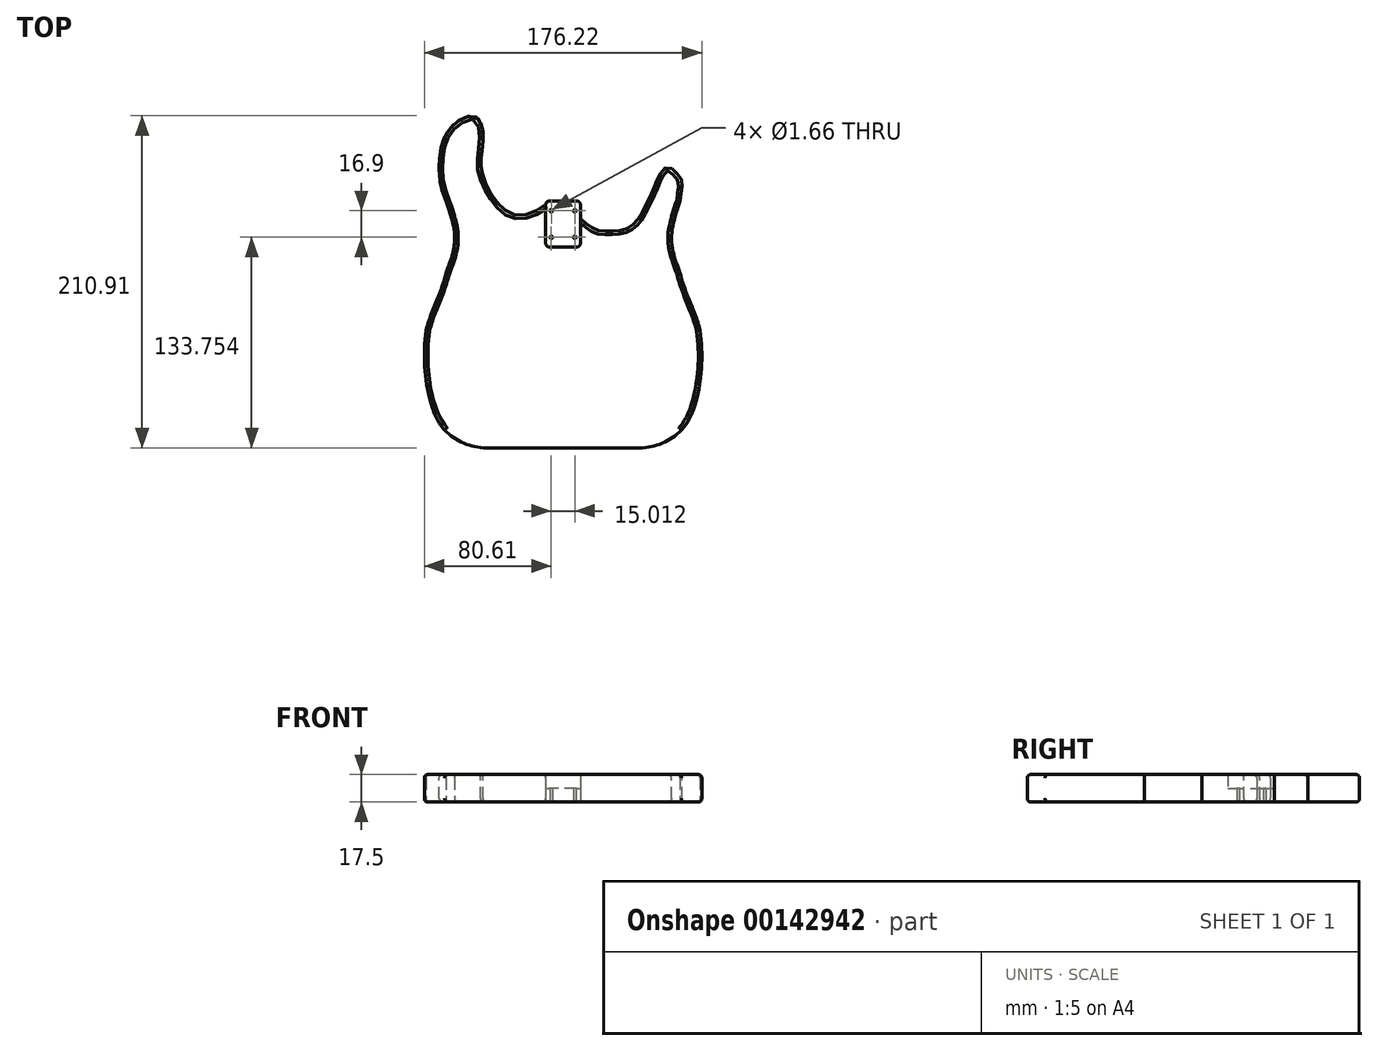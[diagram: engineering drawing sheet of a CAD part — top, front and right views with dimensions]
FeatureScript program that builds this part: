
annotation { "Feature Type Name" : "Feature", "Feature Type Description" : "" }
export const myFeature = defineFeature(function(context is Context, id is Id, definition is map)
    precondition{}
    {
        {
            var Q0;
            Q0=qCreatedBy(makeId("Top.planeOp"),FACE);
            var sketch = newSketch(context, id + "F0", { "sketchPlane" : qUnion([Q0])});
            skLineSegment(sketch, "E0", {"start": v(-48.7, -35.3) * mm, "end": v(0, -35.3) * mm});
            skArc(sketch, "E1", {"start": v(-75.2, -24.05) * mm, "mid": v(-63.1, -32.38) * mm, "end": v(-48.7, -35.3) * mm});
            skLineSegment(sketch, "E2.MirrorCS", {"start": v(48.7, -35.3) * mm, "end": v(0, -35.3) * mm});
            skArc(sketch, "E3.MirrorCS", {"start": v(75.2, -24.05) * mm, "mid": v(63.1, -32.38) * mm, "end": v(48.7, -35.3) * mm});
            skLineSegment(sketch, "E4", {"start": v(0, -35.3) * mm, "end": v(0, 202.55) * mm, "construction": true});
            skLineSegment(sketch, "E5.bottom", {"start": v(8.5, 92.2) * mm, "end": v(-8.5, 92.2) * mm});
            skLineSegment(sketch, "E5.top", {"start": v(8.5, 121.57) * mm, "end": v(-8.5, 121.57) * mm});
            skLineSegment(sketch, "E5.left", {"start": v(11, 94.7) * mm, "end": v(11, 119.07) * mm});
            skLineSegment(sketch, "E5.right", {"start": v(-11, 94.7) * mm, "end": v(-11, 119.07) * mm});
            skPoint(sketch, "E5.middle", {"position": v(0, 106.88) * mm});
            skPoint(sketch, "E6", {"position": v(11, 110.3) * mm});
            skCircle(sketch, "E7", {"center": v(-7.5, 98.44) * mm, "radius": 0.83 * mm});
            skLineSegment(sketch, "E8", {"start": v(-11, 106.9) * mm, "end": v(11, 106.88) * mm, "construction": true});
            skCircle(sketch, "E9.MirrorC", {"center": v(7.5, 98.44) * mm, "radius": 0.83 * mm});
            skLineSegment(sketch, "E10.MirrorCS", {"start": v(11, 106.9) * mm, "end": v(-11, 106.88) * mm, "construction": true});
            skCircle(sketch, "E11.MirrorC", {"center": v(-7.49, 115.34) * mm, "radius": 0.83 * mm});
            skCircle(sketch, "E12.MirrorC", {"center": v(7.51, 115.32) * mm, "radius": 0.83 * mm});
            skFitSpline(sketch, "E13", {"points": [v(-75.2, -24.05) * mm, v(-87, 7.11) * mm, v(-86.97, 39.1) * mm], "startDerivative": vector(-39.42, 41.67) * mm, "endDerivative": vector(8.43, 65.14) * mm});
            skFitSpline(sketch, "E14", {"points": [v(-86.97, 39.1) * mm, v(-74.37, 75.63) * mm], "startDerivative": vector(7.39, 34.16) * mm, "endDerivative": vector(7.39, 34.16) * mm});
            skFitSpline(sketch, "E15", {"points": [v(-74.37, 75.63) * mm, v(-68.78, 97.16) * mm, v(-74.37, 121.57) * mm], "startDerivative": vector(15.15, 40.9) * mm, "endDerivative": vector(-14.7, 44.2) * mm});
            skArc(sketch, "E16.filletArc", {"start": v(-8.5, 121.57) * mm, "mid": v(-10.27, 120.83) * mm, "end": v(-11, 119.07) * mm});
            skPoint(sketch, "E17.visualSharp", {"position": v(11, 121.57) * mm});
            skArc(sketch, "E17.filletArc", {"start": v(11, 119.07) * mm, "mid": v(10.27, 120.83) * mm, "end": v(8.5, 121.57) * mm});
            skPoint(sketch, "E18.visualSharp", {"position": v(11, 92.2) * mm});
            skArc(sketch, "E18.filletArc", {"start": v(8.5, 92.2) * mm, "mid": v(10.27, 92.93) * mm, "end": v(11, 94.7) * mm});
            skPoint(sketch, "E19.visualSharp", {"position": v(-11, 92.2) * mm});
            skArc(sketch, "E19.filletArc", {"start": v(-11, 94.7) * mm, "mid": v(-10.27, 92.93) * mm, "end": v(-8.5, 92.2) * mm});
            skFitSpline(sketch, "E20.MirrorCS", {"points": [v(75.2, -24.05) * mm, v(87, 7.11) * mm, v(86.97, 39.1) * mm], "startDerivative": vector(39.42, 41.67) * mm, "endDerivative": vector(-8.43, 65.14) * mm});
            skFitSpline(sketch, "E21.MirrorCS", {"points": [v(86.97, 39.1) * mm, v(74.37, 75.63) * mm], "startDerivative": vector(-7.39, 34.16) * mm, "endDerivative": vector(-7.39, 34.16) * mm});
            skFitSpline(sketch, "E22.MirrorCS", {"points": [v(74.37, 75.63) * mm, v(68.78, 97.16) * mm, v(74.37, 121.57) * mm], "startDerivative": vector(-15.15, 40.9) * mm, "endDerivative": vector(14.7, 44.2) * mm});
            skFitSpline(sketch, "E23", {"points": [v(11, 110.3) * mm, v(25.36, 102.49) * mm, v(41.99, 104.67) * mm, v(51.43, 116.67) * mm, v(55.26, 124.38) * mm, v(58.72, 132.27) * mm, v(66.07, 142.9) * mm, v(74.37, 136.36) * mm, v(74.37, 121.57) * mm], "startDerivative": vector(160.3, -145.63) * mm, "endDerivative": vector(-32.29, -251.7) * mm});
            skFitSpline(sketch, "E24", {"points": [v(-74.37, 121.57) * mm, v(-78.47, 147.38) * mm, v(-71.25, 168.12) * mm, v(-55.41, 175.04) * mm, v(-50.84, 159.17) * mm, v(-51.84, 140.86) * mm, v(-34.52, 113.98) * mm, v(-19.75, 113.98) * mm, v(-11, 119.07) * mm], "startDerivative": vector(-84.91, 171.62) * mm, "endDerivative": vector(86.78, 63.16) * mm});
            skSolve(sketch);
        }
        {
            var Q0;
            Q0=makeQuery(id+"F0.imprint","IMPRINT",FACE,{"disambiguationData":[TD([[makeQuery(id+"F0.imprint","IMPRINT",EDGE,{"derivedFrom":sQuery(id+"F0.wireOp",EDGE,"E0")}),1.0]])]});
            extrude(context, id + "F1", {"entities" : qUnion([Q0]), "depth" : 17.5 * mm});
        }
        {
            var Q0;
            Q0=makeQuery(id+"F0.imprint","IMPRINT",FACE,{"disambiguationData":[TD([[makeQuery(id+"F0.imprint","IMPRINT",EDGE,{"derivedFrom":sQuery(id+"F0.wireOp",EDGE,"E5.bottom")}),-1.0]])]});
            extrude(context, id + "F2", {"entities" : qUnion([Q0]), "operationType" : NewBodyOperationType.ADD, "depth" : 8.75 * mm});
        }
        {
            var Q0;
            Q0=makeQuery(id+"F1.opExtrude","CAP_EDGE",EDGE,{"disambiguationData":[OSD([sQuery(id+"F0.wireOp",EDGE,"E3.MirrorCS")])],"isStart":false});
            var Q1;
            Q1=makeQuery(id+"F1.opExtrude","CAP_EDGE",EDGE,{"disambiguationData":[OSD([sQuery(id+"F0.wireOp",EDGE,"E20.MirrorCS")])],"isStart":false});
            var Q2;
            Q2=makeQuery(id+"F1.opExtrude","CAP_EDGE",EDGE,{"disambiguationData":[OSD([sQuery(id+"F0.wireOp",EDGE,"E21.MirrorCS")])],"isStart":false});
            var Q3;
            Q3=makeQuery(id+"F1.opExtrude","CAP_EDGE",EDGE,{"disambiguationData":[OSD([sQuery(id+"F0.wireOp",EDGE,"E20.MirrorCS")])],"isStart":true});
            var Q4;
            Q4=makeQuery(id+"F1.opExtrude","CAP_EDGE",EDGE,{"disambiguationData":[OSD([sQuery(id+"F0.wireOp",EDGE,"E21.MirrorCS")])],"isStart":true});
            var Q5;
            Q5=makeQuery(id+"F1.opExtrude","CAP_EDGE",EDGE,{"disambiguationData":[OSD([sQuery(id+"F0.wireOp",EDGE,"E3.MirrorCS")])],"isStart":true});
            var Q6;
            Q6=makeQuery(id+"F1.opExtrude","CAP_EDGE",EDGE,{"disambiguationData":[OSD([sQuery(id+"F0.wireOp",EDGE,"E22.MirrorCS")])],"isStart":true});
            var Q7;
            Q7=makeQuery(id+"F1.opExtrude","CAP_EDGE",EDGE,{"disambiguationData":[OSD([sQuery(id+"F0.wireOp",EDGE,"E22.MirrorCS")])],"isStart":false});
            var Q8;
            Q8=makeQuery(id+"F1.opExtrude","CAP_EDGE",EDGE,{"disambiguationData":[OSD([sQuery(id+"F0.wireOp",EDGE,"E23")])],"isStart":false});
            var Q9;
            Q9=makeQuery(id+"F1.opExtrude","CAP_EDGE",EDGE,{"disambiguationData":[OSD([sQuery(id+"F0.wireOp",EDGE,"E23")])],"isStart":true});
            var Q10;
            Q10=makeQuery(id+"F1.opExtrude","CAP_EDGE",EDGE,{"disambiguationData":[OSD([sQuery(id+"F0.wireOp",EDGE,"E13")])],"isStart":true});
            var Q11;
            Q11=makeQuery(id+"F1.opExtrude","CAP_EDGE",EDGE,{"disambiguationData":[OSD([sQuery(id+"F0.wireOp",EDGE,"E13")])],"isStart":false});
            var Q12;
            Q12=makeQuery(id+"F1.opExtrude","CAP_EDGE",EDGE,{"disambiguationData":[OSD([sQuery(id+"F0.wireOp",EDGE,"E14")])],"isStart":false});
            var Q13;
            Q13=makeQuery(id+"F1.opExtrude","CAP_EDGE",EDGE,{"disambiguationData":[OSD([sQuery(id+"F0.wireOp",EDGE,"E14")])],"isStart":true});
            var Q14;
            Q14=makeQuery(id+"F1.opExtrude","CAP_EDGE",EDGE,{"disambiguationData":[OSD([sQuery(id+"F0.wireOp",EDGE,"E15")])],"isStart":true});
            var Q15;
            Q15=makeQuery(id+"F1.opExtrude","CAP_EDGE",EDGE,{"disambiguationData":[OSD([sQuery(id+"F0.wireOp",EDGE,"E15")])],"isStart":false});
            var Q16;
            Q16=makeQuery(id+"F1.opExtrude","CAP_EDGE",EDGE,{"disambiguationData":[OSD([sQuery(id+"F0.wireOp",EDGE,"9ea45a0f-3cd6-4a9c-9ebc-cc36737b0496")])],"isStart":true});
            var Q17;
            Q17=makeQuery(id+"F1.opExtrude","CAP_EDGE",EDGE,{"disambiguationData":[OSD([sQuery(id+"F0.wireOp",EDGE,"9ea45a0f-3cd6-4a9c-9ebc-cc36737b0496")])],"isStart":false});
            var Q18;
            Q18=makeQuery(id+"F1.opExtrude","CAP_EDGE",EDGE,{"disambiguationData":[OSD([sQuery(id+"F0.wireOp",EDGE,"E24")])],"isStart":false});
            var Q19;
            Q19=makeQuery(id+"F1.opExtrude","CAP_EDGE",EDGE,{"disambiguationData":[OSD([sQuery(id+"F0.wireOp",EDGE,"E24")])],"isStart":true});
            fillet(context, id + "F3", {"entities" : qUnion([Q0, Q1, Q2, Q3, Q4, Q5, Q6, Q7, Q8, Q9, Q10, Q11, Q12, Q13, Q14, Q15, Q16, Q17, Q18, Q19]), "radius" : 2.2 * mm, "tangentPropagation" : true, "allowEdgeOverflow" : false});
        }
    });
